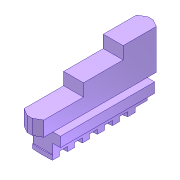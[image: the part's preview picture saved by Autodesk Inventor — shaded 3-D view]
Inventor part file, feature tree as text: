
AUTODESK INVENTOR PART (.ipt)
format: ipt  version: 2016 (Build 200138000, 138)  size: 251,392 bytes
history: native  units: in
note: dims shown in document units (in); Inventor stores cm internally (conversion verified against a paired STEP export)
features: extrude x7, sketch x7, fillet x1, projected_geometry x1
ambient origin geometry x8: Origin, YZ Plane, XZ Plane, XY Plane, X Axis, Y Axis, Z Axis, Center Point
bodies: Solid1 (feature_tree)
feature tree (16):
  extrude  "Extrusion8"  Depth=0.1378in
  extrude  "Extrusion9"  Depth=0.0787in
  extrude  "Extrusion10"  Depth=0.315in
  extrude  "Extrusion11"  TaperAngle=30.0deg  [1 undecoded]
  extrude  "Extrusion13"  Depth=0.7874in TaperAngle=0.0deg
  extrude  "Extrusion14"  Depth=0.1969in TaperAngle=0.0deg
  fillet  "Fillet1"  Radius=0.315in
  extrude  "Extrusion16"  Depth=0.1181in
  sketch  "Sketch10"  dims[d51=0.0787in d52=0.1378in]
  sketch  "Sketch11"  dims[d53=0.0787in d54=0.0787in]
  sketch  "Sketch12"  dims[d55=0.0787in d56=0.315in]
  sketch  "Sketch13"  dims[d57=0.9843in d58=0.0in d59=30.0deg]
  sketch  "Sketch15"  dims[d60=30.0deg d61=0.7874in d62=0.0in]
  sketch  "Sketch16"  dims[d63=0.315in d64=0.1969in d65=0.0in d66=0.315in]
  sketch  "Sketch18"  dims[d67=0.0984in d68=0.0in d72=0.1181in d73=0.1181in d74=0.0787in d75=0.0in d76=0.4567in d79=0.0551in d81=0.0551in d83=0.0551in d85=0.0551in d87=0.0551in d89=0.0551in d90=0.0354in d91=0.0in d92=0.1181in d93=0.1181in d94=0.1181in d95=0.1181in d96=0.1181in d102=0.0008in d103=0.0118in d104=0.0118in d105=0.3937in d106=0.0in]
  projected_geometry  "Projected Loop1"
note: 1 required parameter value undecoded (feature->parameter linkage not recoverable at this tier; creation-order binding heuristic only, values carry confidence <= 0.55)
